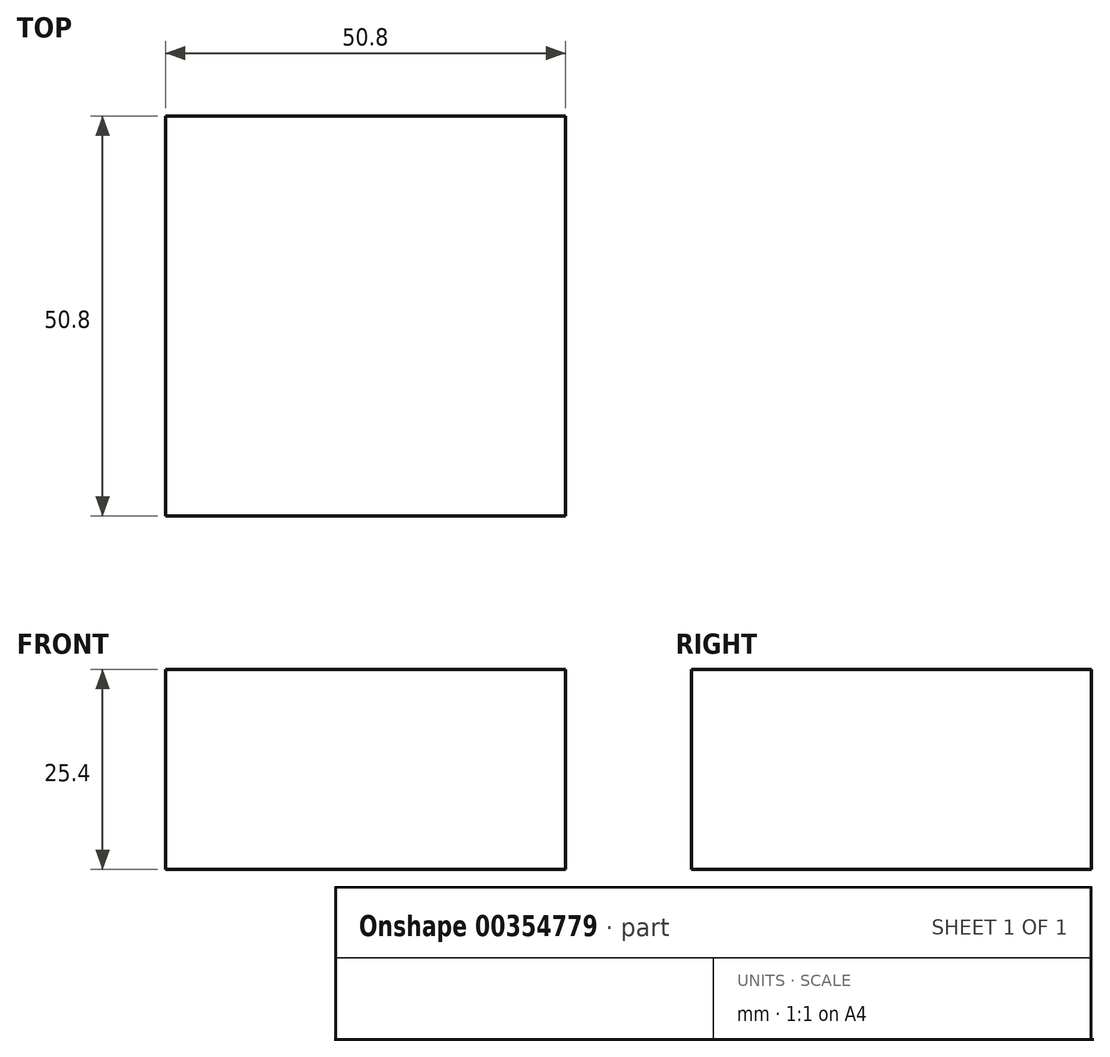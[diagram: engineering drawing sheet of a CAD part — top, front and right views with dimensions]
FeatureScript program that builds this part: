
annotation { "Feature Type Name" : "Feature", "Feature Type Description" : "" }
export const myFeature = defineFeature(function(context is Context, id is Id, definition is map)
    precondition{}
    {
        {
            var Q0;
            Q0=qCreatedBy(makeId("Top.planeOp"),FACE);
            var sketch = newSketch(context, id + "F0", { "sketchPlane" : qUnion([Q0])});
            skLineSegment(sketch, "E0.bottom", {"start": v(25.4, -25.4) * mm, "end": v(-25.4, -25.4) * mm});
            skLineSegment(sketch, "E0.top", {"start": v(25.4, 25.4) * mm, "end": v(-25.4, 25.4) * mm});
            skLineSegment(sketch, "E0.left", {"start": v(25.4, -25.4) * mm, "end": v(25.4, 25.4) * mm});
            skLineSegment(sketch, "E0.right", {"start": v(-25.4, -25.4) * mm, "end": v(-25.4, 25.4) * mm});
            skPoint(sketch, "E0.middle", {"position": v(0, 0) * mm});
            skSolve(sketch);
        }
        {
            var Q0;
            Q0=makeQuery(id+"F0.imprint","IMPRINT",FACE,{"disambiguationData":[TD([[makeQuery(id+"F0.imprint","IMPRINT",EDGE,{"derivedFrom":sQuery(id+"F0.wireOp",EDGE,"E0.bottom")}),-1.0]])]});
            extrude(context, id + "F1", {"entities" : qUnion([Q0]), "depth" : 25.4 * mm});
        }
    });
